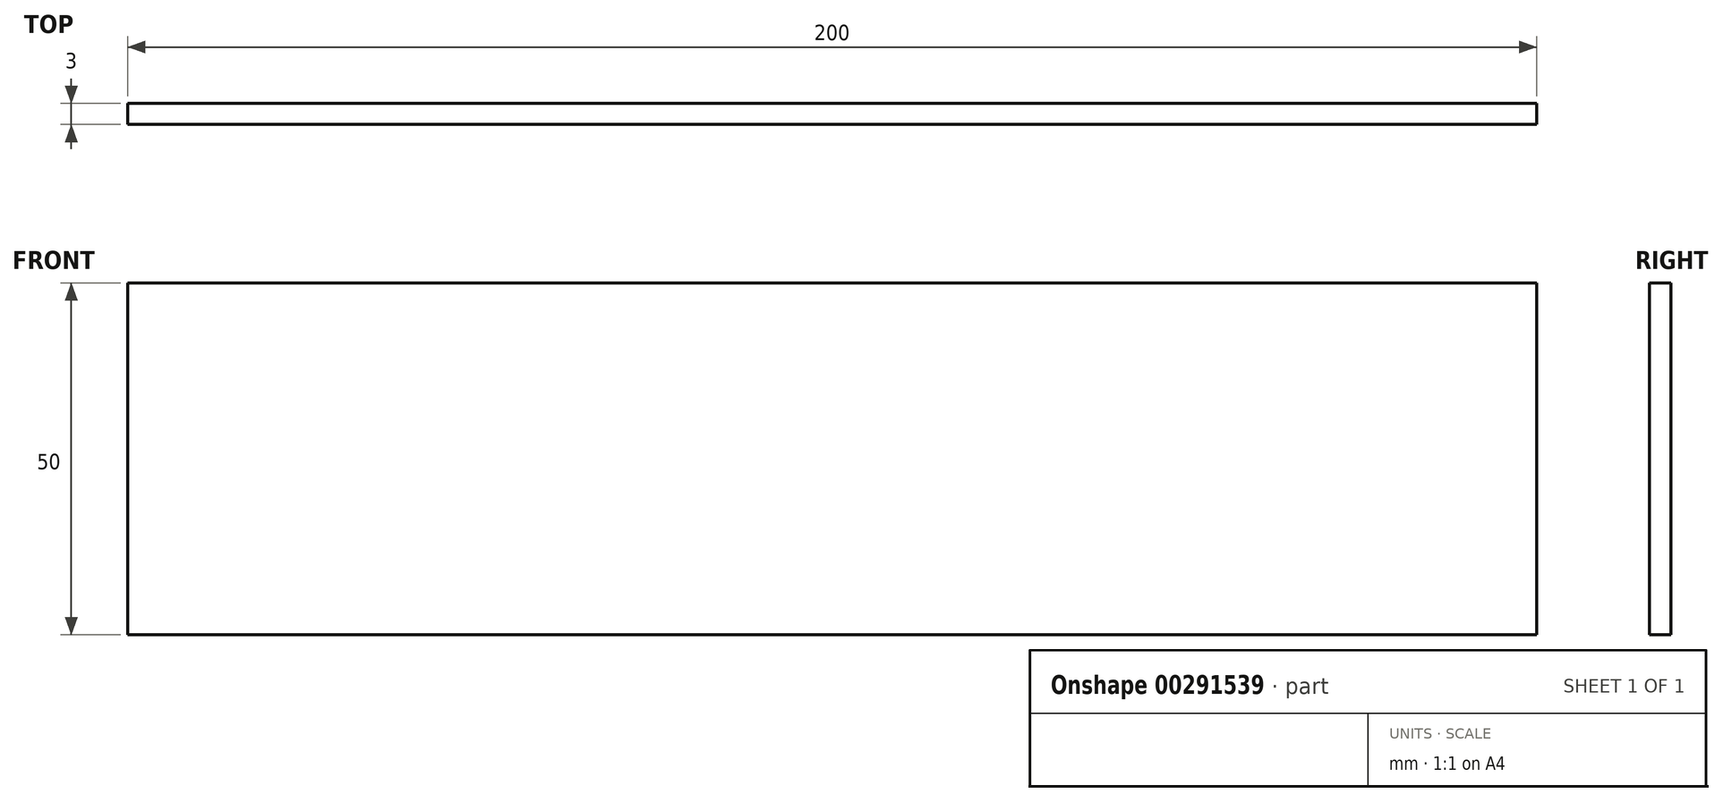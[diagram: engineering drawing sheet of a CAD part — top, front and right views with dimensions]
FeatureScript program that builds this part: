
annotation { "Feature Type Name" : "Feature", "Feature Type Description" : "" }
export const myFeature = defineFeature(function(context is Context, id is Id, definition is map)
    precondition{}
    {
        {
            var Q0;
            Q0=qCreatedBy(makeId("Front.planeOp"),FACE);
            var sketch = newSketch(context, id + "F0", { "sketchPlane" : qUnion([Q0])});
            skLineSegment(sketch, "E0.bottom", {"start": v(-100, 25) * mm, "end": v(100, 25) * mm});
            skLineSegment(sketch, "E0.top", {"start": v(-100, -25) * mm, "end": v(100, -25) * mm});
            skLineSegment(sketch, "E0.left", {"start": v(-100, 25) * mm, "end": v(-100, -25) * mm});
            skLineSegment(sketch, "E0.right", {"start": v(100, 25) * mm, "end": v(100, -25) * mm});
            skSolve(sketch);
        }
        {
            var Q0;
            Q0=makeQuery(id+"F0.imprint","IMPRINT",FACE,{"disambiguationData":[TD([[makeQuery(id+"F0.imprint","IMPRINT",EDGE,{"derivedFrom":sQuery(id+"F0.wireOp",EDGE,"E0.bottom")}),-1.0]])]});
            extrude(context, id + "F1", {"entities" : qUnion([Q0]), "endBound" : BoundingType.SYMMETRIC, "depth" : 3 * mm});
        }
    });
